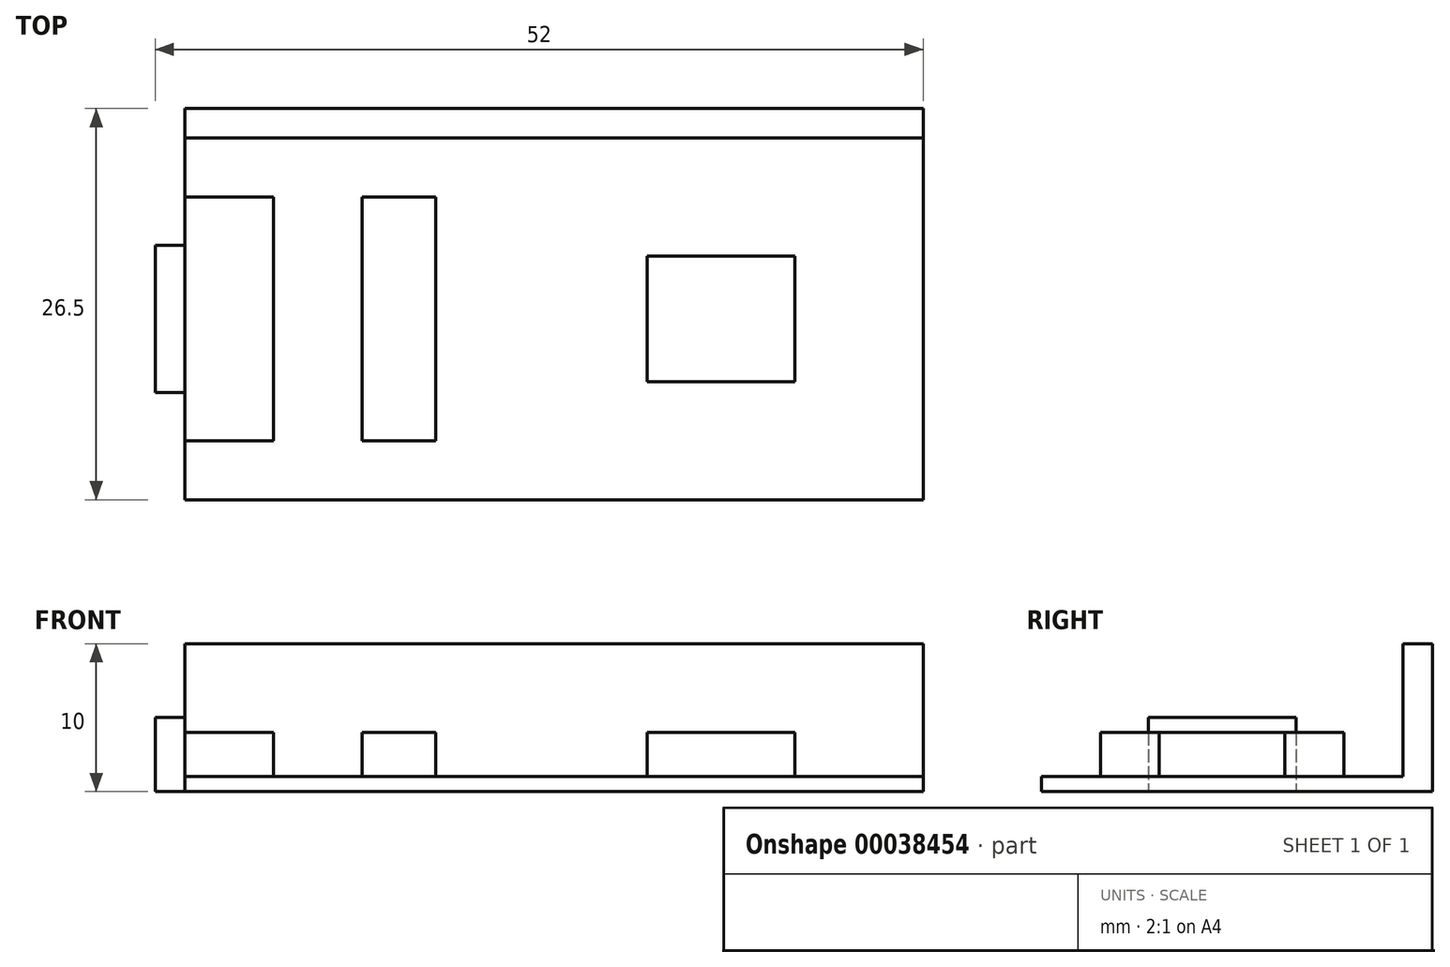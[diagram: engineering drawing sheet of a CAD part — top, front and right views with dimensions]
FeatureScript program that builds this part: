
annotation { "Feature Type Name" : "Feature", "Feature Type Description" : "" }
export const myFeature = defineFeature(function(context is Context, id is Id, definition is map)
    precondition{}
    {
        {
            var Q0;
            Q0=qCreatedBy(makeId("Top.planeOp"),FACE);
            var sketch = newSketch(context, id + "F0", { "sketchPlane" : qUnion([Q0])});
            skLineSegment(sketch, "E0.bottom", {"start": v(0, 0) * mm, "end": v(52, 0) * mm});
            skLineSegment(sketch, "E0.top", {"start": v(0, 28.5) * mm, "end": v(52, 28.5) * mm});
            skLineSegment(sketch, "E0.left", {"start": v(0, 0) * mm, "end": v(0, 28.5) * mm});
            skLineSegment(sketch, "E0.right", {"start": v(52, 0) * mm, "end": v(52, 28.5) * mm});
            skLineSegment(sketch, "E1.bottom", {"start": v(0, 28.5) * mm, "end": v(2, 28.5) * mm});
            skLineSegment(sketch, "E1.top", {"start": v(0, 0) * mm, "end": v(2, 0) * mm});
            skLineSegment(sketch, "E1.left", {"start": v(0, 28.5) * mm, "end": v(0, 0) * mm});
            skLineSegment(sketch, "E1.right", {"start": v(2, 28.5) * mm, "end": v(2, 0) * mm});
            skLineSegment(sketch, "E2.bottom", {"start": v(2, 26.5) * mm, "end": v(52, 26.5) * mm});
            skLineSegment(sketch, "E2.top", {"start": v(2, 28.5) * mm, "end": v(52, 28.5) * mm});
            skLineSegment(sketch, "E2.left", {"start": v(2, 26.5) * mm, "end": v(2, 28.5) * mm});
            skLineSegment(sketch, "E2.right", {"start": v(52, 26.5) * mm, "end": v(52, 28.5) * mm});
            skLineSegment(sketch, "E3.bottom", {"start": v(2, 0) * mm, "end": v(52, 0) * mm});
            skLineSegment(sketch, "E3.top", {"start": v(2, 2) * mm, "end": v(52, 2) * mm});
            skLineSegment(sketch, "E3.left", {"start": v(2, 0) * mm, "end": v(2, 2) * mm});
            skLineSegment(sketch, "E3.right", {"start": v(52, 0) * mm, "end": v(52, 2) * mm});
            skLineSegment(sketch, "E4", {"start": v(-6.31, 22.5) * mm, "end": v(72.94, 22.5) * mm, "construction": true});
            skLineSegment(sketch, "E5", {"start": v(-7.44, 6) * mm, "end": v(76.56, 6) * mm, "construction": true});
            skLineSegment(sketch, "E6.top", {"start": v(52, 6) * mm, "end": v(71, 6) * mm});
            skLineSegment(sketch, "E7.bottom", {"start": v(2, 22.5) * mm, "end": v(8, 22.5) * mm});
            skLineSegment(sketch, "E7.top", {"start": v(2, 6) * mm, "end": v(8, 6) * mm});
            skLineSegment(sketch, "E7.left", {"start": v(2, 22.5) * mm, "end": v(2, 6) * mm});
            skLineSegment(sketch, "E7.right", {"start": v(8, 22.5) * mm, "end": v(8, 6) * mm});
            skLineSegment(sketch, "E8.bottom", {"start": v(14, 22.5) * mm, "end": v(19, 22.5) * mm});
            skLineSegment(sketch, "E8.top", {"start": v(14, 6) * mm, "end": v(19, 6) * mm});
            skLineSegment(sketch, "E8.left", {"start": v(14, 22.5) * mm, "end": v(14, 6) * mm});
            skLineSegment(sketch, "E8.right", {"start": v(19, 22.5) * mm, "end": v(19, 6) * mm});
            skLineSegment(sketch, "E9.bottom", {"start": v(33.3, 18.5) * mm, "end": v(43.3, 18.5) * mm});
            skLineSegment(sketch, "E9.top", {"start": v(33.3, 10) * mm, "end": v(43.3, 10) * mm});
            skLineSegment(sketch, "E9.left", {"start": v(33.3, 18.5) * mm, "end": v(33.3, 10) * mm});
            skLineSegment(sketch, "E9.right", {"start": v(43.3, 18.5) * mm, "end": v(43.3, 10) * mm});
            skLineSegment(sketch, "E10.bottom", {"start": v(0, 19.25) * mm, "end": v(2, 19.25) * mm});
            skLineSegment(sketch, "E10.top", {"start": v(0, 9.25) * mm, "end": v(2, 9.25) * mm});
            skLineSegment(sketch, "E10.left", {"start": v(0, 19.25) * mm, "end": v(0, 9.25) * mm});
            skLineSegment(sketch, "E10.right", {"start": v(2, 19.25) * mm, "end": v(2, 9.25) * mm});
            skLineSegment(sketch, "E11", {"start": v(2, 14.25) * mm, "end": v(0, 14.25) * mm, "construction": true});
            skPoint(sketch, "E11.endSnap0", {"position": v(2, 14.25) * mm});
            skLineSegment(sketch, "E12.left", {"start": v(52, 28.5) * mm, "end": v(52, 0) * mm});
            skSolve(sketch);
        }
        {
            var Q0;
            {var subQ0=sQuery(id+"F0.wireOp",EDGE,"E6.bottom");Q0=makeQuery(id+"F0.imprint","IMPRINT",FACE,{"disambiguationData":[TD([[makeQuery(id+"F0.imprint","IMPRINT",EDGE,{"derivedFrom":subQ0}),-1.0]])]});}
            var Q1;
            {var subQ7=sQuery(id+"F0.wireOp",EDGE,"E2.bottom");Q1=makeQuery(id+"F0.imprint","IMPRINT",FACE,{"disambiguationData":[TD([[makeQuery(id+"F0.imprint","IMPRINT",EDGE,{"derivedFrom":subQ7}),-1.0]])]});}
            var Q2;
            Q2=makeQuery(id+"F0.imprint","IMPRINT",FACE,{"disambiguationData":[TD([[makeQuery(id+"F0.imprint","IMPRINT",EDGE,{"derivedFrom":sQuery(id+"F0.wireOp",EDGE,"E6.right")}),1.0]])]});
            extrude(context, id + "F1", {"entities" : qUnion([Q0, Q1, Q2]), "depth" : 1 * mm});
        }
        {
            var Q0;
            {var subQ4=sQuery(id+"F0.wireOp",EDGE,"E7.bottom");Q0=makeQuery(id+"F0.imprint","IMPRINT",FACE,{"disambiguationData":[TD([[makeQuery(id+"F0.imprint","IMPRINT",EDGE,{"derivedFrom":subQ4}),-1.0]])]});}
            var Q1;
            Q1=makeQuery(id+"F0.imprint","IMPRINT",FACE,{"disambiguationData":[TD([[makeQuery(id+"F0.imprint","IMPRINT",EDGE,{"derivedFrom":sQuery(id+"F0.wireOp",EDGE,"E8.bottom")}),-1.0]])]});
            var Q2;
            Q2=makeQuery(id+"F0.imprint","IMPRINT",FACE,{"disambiguationData":[TD([[makeQuery(id+"F0.imprint","IMPRINT",EDGE,{"derivedFrom":sQuery(id+"F0.wireOp",EDGE,"E9.bottom")}),-1.0]])]});
            extrude(context, id + "F2", {"entities" : qUnion([Q0, Q1, Q2]), "operationType" : NewBodyOperationType.ADD, "depth" : 4 * mm});
        }
        {
            var Q0;
            Q0=makeQuery(id+"F0.imprint","IMPRINT",FACE,{"disambiguationData":[TD([[makeQuery(id+"F0.imprint","IMPRINT",EDGE,{"derivedFrom":sQuery(id+"F0.wireOp",EDGE,"E10.bottom")}),-1.0]])]});
            extrude(context, id + "F3", {"entities" : qUnion([Q0]), "operationType" : NewBodyOperationType.ADD, "depth" : 5 * mm});
        }
        {
            var Q0;
            Q0=makeQuery(id+"F0.imprint","IMPRINT",FACE,{"disambiguationData":[TD([[makeQuery(id+"F0.imprint","IMPRINT",EDGE,{"derivedFrom":sQuery(id+"F0.wireOp",EDGE,"E2.bottom")}),1.0]])]});
            var Q1;
            {var subQ5=sQuery(id+"F0.wireOp",EDGE,"E1.bottom");Q1=makeQuery(id+"F0.imprint","IMPRINT",FACE,{"disambiguationData":[TD([[makeQuery(id+"F0.imprint","IMPRINT",EDGE,{"derivedFrom":subQ5}),-1.0]])]});}
            var Q2;
            {var subQ5=sQuery(id+"F0.wireOp",EDGE,"E1.top");Q2=makeQuery(id+"F0.imprint","IMPRINT",FACE,{"disambiguationData":[TD([[makeQuery(id+"F0.imprint","IMPRINT",EDGE,{"derivedFrom":subQ5}),1.0]])]});}
            var Q3;
            Q3=makeQuery(id+"F0.imprint","IMPRINT",FACE,{"disambiguationData":[TD([[makeQuery(id+"F0.imprint","IMPRINT",EDGE,{"derivedFrom":sQuery(id+"F0.wireOp",EDGE,"E3.bottom")}),1.0]])]});
            extrude(context, id + "F4", {"entities" : qUnion([Q0, Q1, Q2, Q3]), "operationType" : NewBodyOperationType.ADD, "depth" : 10 * mm});
        }
    });
